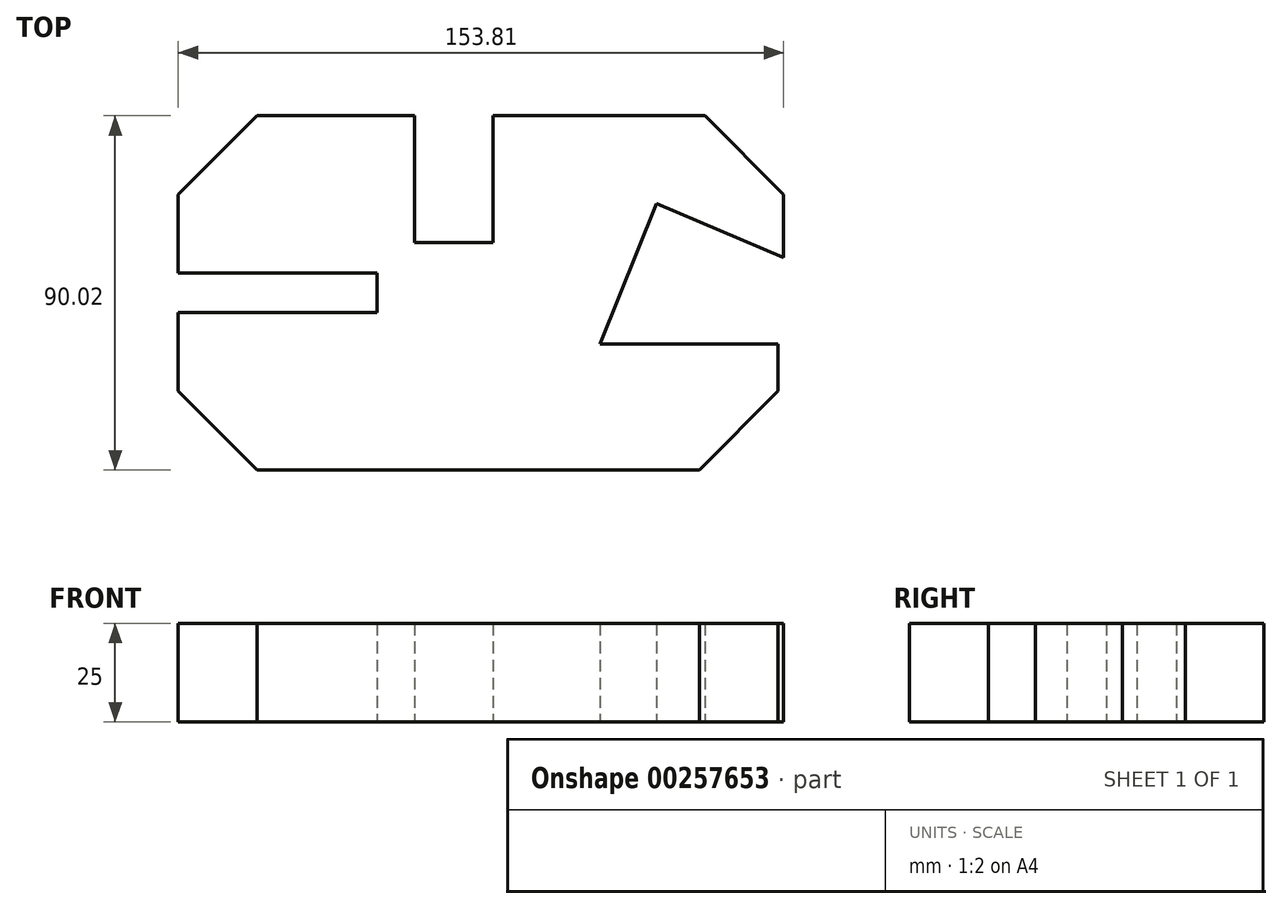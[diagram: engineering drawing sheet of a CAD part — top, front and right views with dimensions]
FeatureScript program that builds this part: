
annotation { "Feature Type Name" : "Feature", "Feature Type Description" : "" }
export const myFeature = defineFeature(function(context is Context, id is Id, definition is map)
    precondition{}
    {
        {
            var Q0;
            Q0=qCreatedBy(makeId("Top.planeOp"),FACE);
            var sketch = newSketch(context, id + "F0", { "sketchPlane" : qUnion([Q0])});
            skLineSegment(sketch, "E0", {"start": v(-60, -67.7) * mm, "end": v(52.4, -67.7) * mm});
            skLineSegment(sketch, "E1", {"start": v(-60, -67.7) * mm, "end": v(-80.01, -47.7) * mm});
            skLineSegment(sketch, "E2", {"start": v(-80.01, -47.7) * mm, "end": v(-80.01, -27.7) * mm});
            skLineSegment(sketch, "E3", {"start": v(-80.01, -27.7) * mm, "end": v(-29.51, -27.7) * mm});
            skLineSegment(sketch, "E4", {"start": v(-29.51, -27.7) * mm, "end": v(-29.51, -17.7) * mm});
            skLineSegment(sketch, "E5", {"start": v(-29.51, -17.7) * mm, "end": v(-80.01, -17.7) * mm});
            skLineSegment(sketch, "E6", {"start": v(-80.01, -17.7) * mm, "end": v(-80.01, 2.3) * mm});
            skLineSegment(sketch, "E7", {"start": v(-80.01, 2.3) * mm, "end": v(-60, 22.31) * mm});
            skLineSegment(sketch, "E8", {"start": v(-60, 22.31) * mm, "end": v(-20, 22.31) * mm});
            skLineSegment(sketch, "E9", {"start": v(-20, 22.31) * mm, "end": v(-20, -9.99) * mm});
            skLineSegment(sketch, "E10", {"start": v(-20, -9.99) * mm, "end": v(0, -9.99) * mm});
            skLineSegment(sketch, "E11", {"start": v(0, -9.99) * mm, "end": v(0, 22.31) * mm});
            skLineSegment(sketch, "E12", {"start": v(53.79, 22.31) * mm, "end": v(73.8, 2.3) * mm});
            skLineSegment(sketch, "E13", {"start": v(73.8, 2.3) * mm, "end": v(73.8, -13.7) * mm});
            skLineSegment(sketch, "E14", {"start": v(52.4, -67.7) * mm, "end": v(72.41, -47.7) * mm});
            skLineSegment(sketch, "E15", {"start": v(72.41, -47.7) * mm, "end": v(72.41, -35.7) * mm});
            skLineSegment(sketch, "E16", {"start": v(72.41, -35.7) * mm, "end": v(27.11, -35.7) * mm});
            skLineSegment(sketch, "E17", {"start": v(27.11, -35.7) * mm, "end": v(41.53, 0) * mm});
            skLineSegment(sketch, "E18", {"start": v(41.53, 0) * mm, "end": v(73.8, -13.7) * mm});
            skLineSegment(sketch, "E19", {"start": v(0, 22.31) * mm, "end": v(53.79, 22.31) * mm});
            skSolve(sketch);
        }
        {
            var Q0;
            Q0 = qSketchRegion(id + "F0", true);
            extrude(context, id + "F1", {"entities" : qUnion([Q0]), "depth" : 25 * mm});
        }
        {
            var Q0;
            Q0 = qSketchRegion(id + "F0", true);
            extrude(context, id + "F2", {"entities" : qUnion([Q0]), "operationType" : NewBodyOperationType.ADD, "depth" : 25 * mm});
        }
    });
